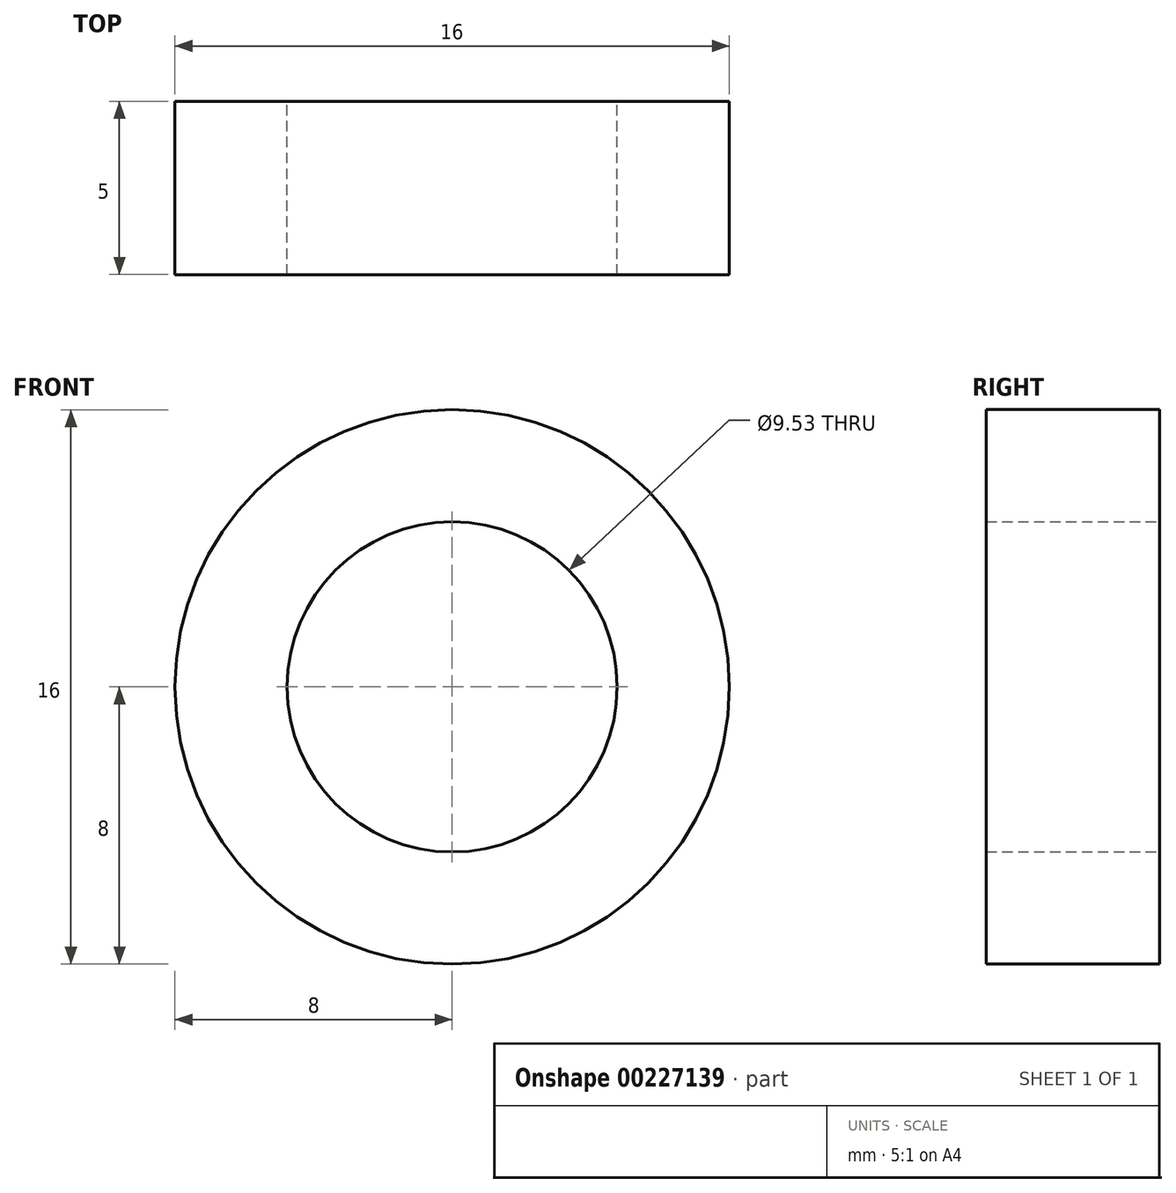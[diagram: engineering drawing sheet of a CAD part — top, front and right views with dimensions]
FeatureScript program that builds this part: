
annotation { "Feature Type Name" : "Feature", "Feature Type Description" : "" }
export const myFeature = defineFeature(function(context is Context, id is Id, definition is map)
    precondition{}
    {
        {
            var Q0;
            Q0=qCreatedBy(makeId("Front.planeOp"),FACE);
            var sketch = newSketch(context, id + "F0", { "sketchPlane" : qUnion([Q0])});
            skCircle(sketch, "E0", {"center": v(0, 0) * mm, "radius": 4.76 * mm});
            skCircle(sketch, "E1", {"center": v(0, 0) * mm, "radius": 8 * mm});
            skSolve(sketch);
        }
        {
            var Q0;
            Q0=makeQuery(id+"F0.imprint","IMPRINT",FACE,{"disambiguationData":[TD([[makeQuery(id+"F0.imprint","IMPRINT",EDGE,{"derivedFrom":sQuery(id+"F0.wireOp",EDGE,"E0")}),-1.0]])]});
            extrude(context, id + "F1", {"entities" : qUnion([Q0]), "depth" : 5 * mm});
        }
    });
